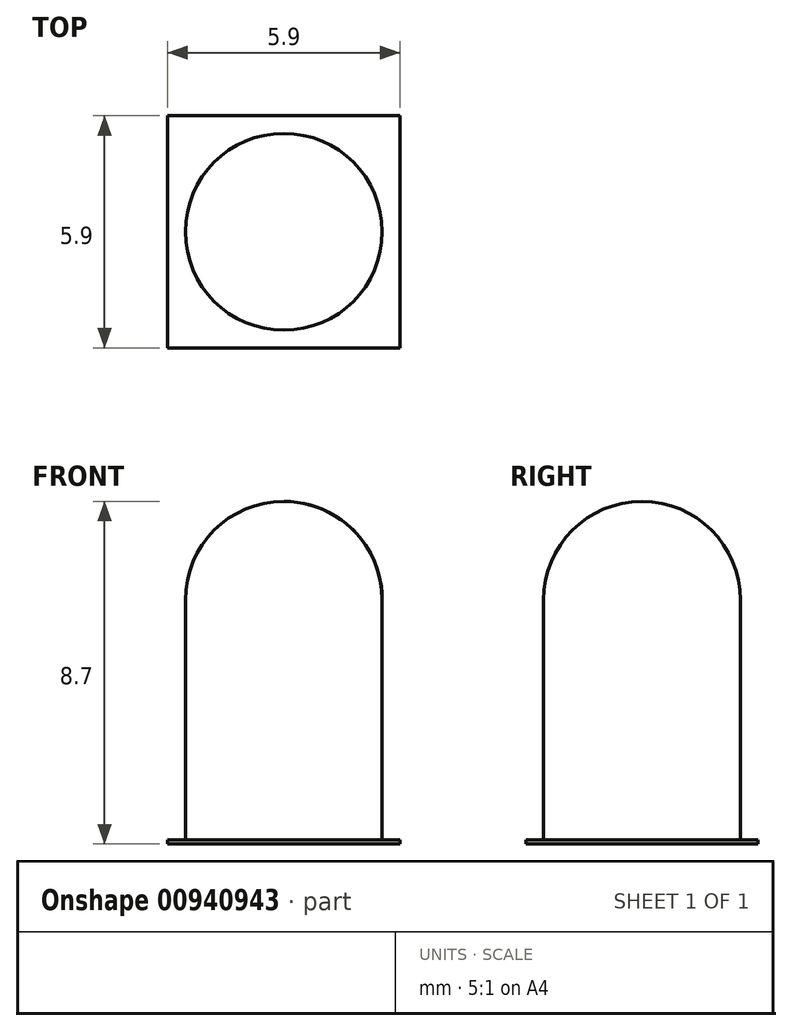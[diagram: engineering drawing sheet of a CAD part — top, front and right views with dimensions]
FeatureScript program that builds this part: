
annotation { "Feature Type Name" : "Feature", "Feature Type Description" : "" }
export const myFeature = defineFeature(function(context is Context, id is Id, definition is map)
    precondition{}
    {
        {
            var Q0;
            Q0=qCreatedBy(makeId("Top.planeOp"),FACE);
            var sketch = newSketch(context, id + "F0", { "sketchPlane" : qUnion([Q0])});
            skCircle(sketch, "E0", {"center": v(0, 0) * mm, "radius": 2.5 * mm});
            skLineSegment(sketch, "E1.bottom", {"start": v(2.95, 2.95) * mm, "end": v(-2.95, 2.95) * mm});
            skLineSegment(sketch, "E1.top", {"start": v(2.95, -2.95) * mm, "end": v(-2.95, -2.95) * mm});
            skLineSegment(sketch, "E1.left", {"start": v(2.95, 2.95) * mm, "end": v(2.95, -2.95) * mm});
            skLineSegment(sketch, "E1.right", {"start": v(-2.95, 2.95) * mm, "end": v(-2.95, -2.95) * mm});
            skSolve(sketch);
        }
        {
            var Q0;
            Q0=qSketchRegion(id+"F0",true);
            extrude(context, id + "F1", {"entities" : qUnion([Q0]), "depth" : 0.1 * mm, "offsetDistance" : 25 * mm});
        }
        {
            var Q0;
            Q0=makeQuery(id+"F0.imprint","IMPRINT",FACE,{"disambiguationData":[TD([[makeQuery(id+"F0.imprint","IMPRINT",EDGE,{"derivedFrom":sQuery(id+"F0.wireOp",EDGE,"E0")}),1.0]])]});
            extrude(context, id + "F2", {"entities" : qUnion([Q0]), "operationType" : NewBodyOperationType.ADD, "depth" : 8.7 * mm, "offsetDistance" : 25 * mm});
        }
        {
            var Q0;
            Q0=makeQuery(id+"F2.opExtrude","CAP_EDGE",EDGE,{"disambiguationData":[OSD([sQuery(id+"F0.wireOp",EDGE,"E0")])],"isStart":false});
            fillet(context, id + "F3", {"entities" : qUnion([Q0]), "radius" : 2.5 * mm, "tangentPropagation" : true, "allowEdgeOverflow" : false});
        }
    });
